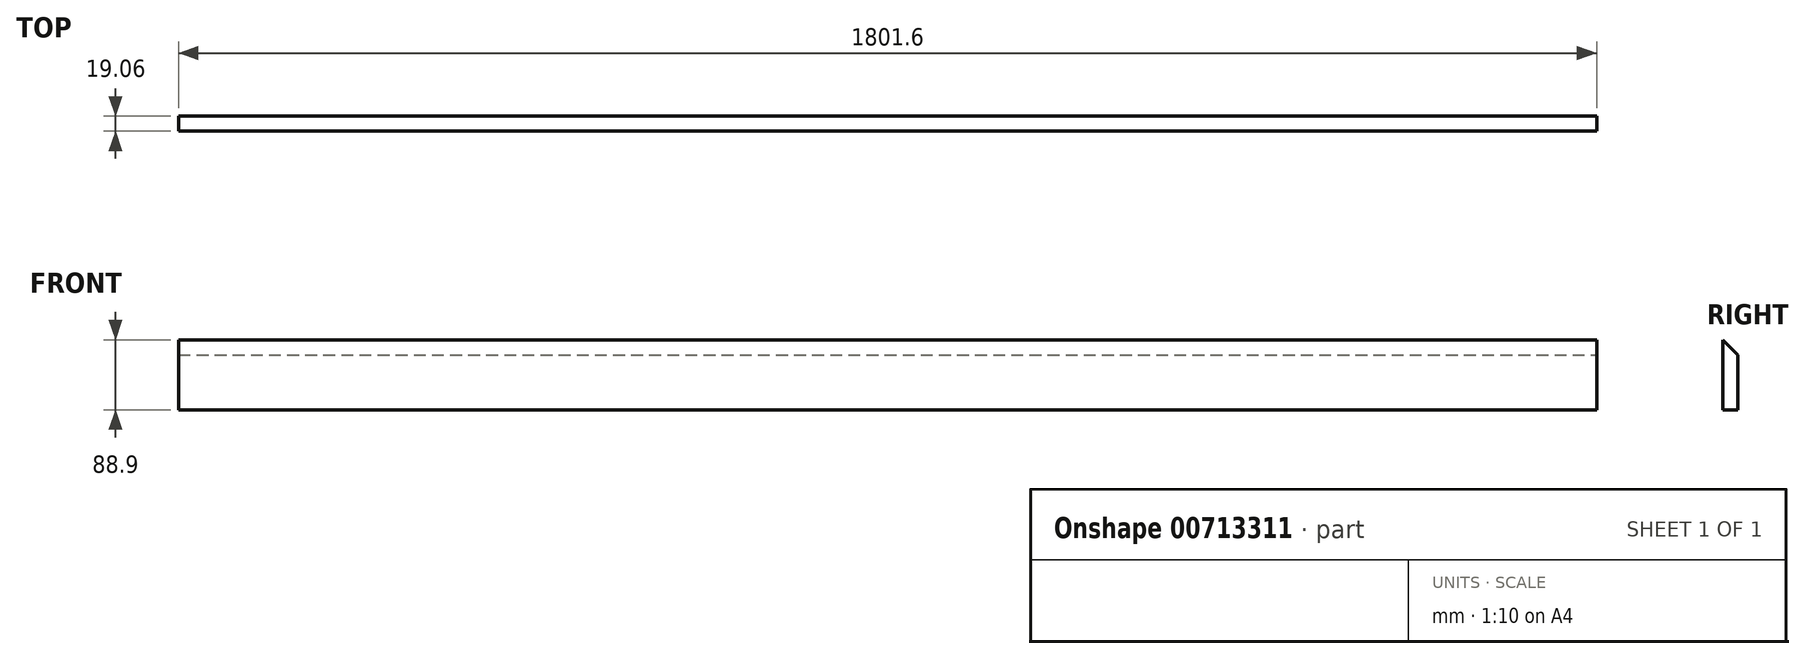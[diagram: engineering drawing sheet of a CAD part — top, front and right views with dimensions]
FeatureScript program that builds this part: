
annotation { "Feature Type Name" : "Feature", "Feature Type Description" : "" }
export const myFeature = defineFeature(function(context is Context, id is Id, definition is map)
    precondition{}
    {
        {
            var Q0;
            Q0=qCreatedBy(makeId("Front.planeOp"),FACE);
            var sketch = newSketch(context, id + "F0", { "sketchPlane" : qUnion([Q0])});
            skLineSegment(sketch, "E0.bottom", {"start": v(900.8, -44.45) * mm, "end": v(-900.8, -44.45) * mm});
            skLineSegment(sketch, "E0.top", {"start": v(900.8, 44.45) * mm, "end": v(-900.8, 44.45) * mm});
            skLineSegment(sketch, "E0.left", {"start": v(900.8, -44.45) * mm, "end": v(900.8, 44.45) * mm});
            skLineSegment(sketch, "E0.right", {"start": v(-900.8, -44.45) * mm, "end": v(-900.8, 44.45) * mm});
            skPoint(sketch, "E0.middle", {"position": v(0, 0) * mm});
            skSolve(sketch);
        }
        {
            var Q0;
            Q0=makeQuery(id+"F0.imprint","IMPRINT",FACE,{"disambiguationData":[TD([[makeQuery(id+"F0.imprint","IMPRINT",EDGE,{"derivedFrom":sQuery(id+"F0.wireOp",EDGE,"E0.bottom")}),-1.0]])]});
            extrude(context, id + "F1", {"entities" : qUnion([Q0]), "endBound" : BoundingType.SYMMETRIC, "depth" : 19.05 * mm, "offsetDistance" : 25.4 * mm});
        }
        {
            var Q0;
            Q0=makeQuery(id+"F1.opExtrude","CAP_EDGE",EDGE,{"disambiguationData":[OSD([sQuery(id+"F0.wireOp",EDGE,"E0.top")])],"isStart":true});
            chamfer(context, id + "F2", {"entities" : qUnion([Q0]), "width" : 19.05 * mm, "tangentPropagation" : true});
        }
    });
